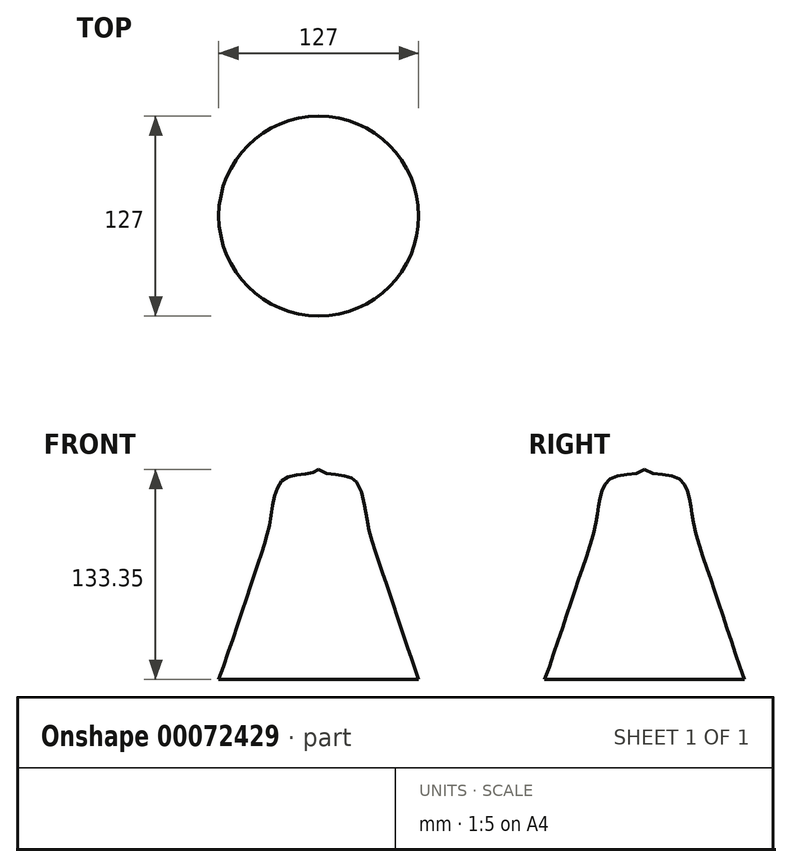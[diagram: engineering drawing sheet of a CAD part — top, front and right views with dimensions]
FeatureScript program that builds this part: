
annotation { "Feature Type Name" : "Feature", "Feature Type Description" : "" }
export const myFeature = defineFeature(function(context is Context, id is Id, definition is map)
    precondition{}
    {
        {
            var Q0;
            Q0=qCreatedBy(makeId("Front.planeOp"),FACE);
            var sketch = newSketch(context, id + "F0", { "sketchPlane" : qUnion([Q0])});
            skLineSegment(sketch, "E0", {"start": v(0, 58.39) * mm, "end": v(0, -74.96) * mm, "construction": true});
            skLineSegment(sketch, "E1.0", {"start": v(-63.5, 76.01) * mm, "end": v(-63.5, -74.96) * mm, "construction": true});
            skFitSpline(sketch, "E2", {"points": [v(-63.5, -74.96) * mm, v(-41.1, -8.94) * mm, v(-30.6, 26.81) * mm, v(-21.34, 52.67) * mm, v(0, 58.39) * mm], "startDerivative": vector(68.52, 189.13) * mm, "endDerivative": vector(57.47, 66.35) * mm});
            skSolve(sketch);
        }
        {
            var Q0;
            Q0=sQuery(id+"F0.wireOp",EDGE,"E2");
            var Q1;
            Q1=sQuery(id+"F0.wireOp",EDGE,"E0");
            revolve(context, id + "F1", {"bodyType" : ToolBodyType.SURFACE, "surfaceEntities" : qUnion([Q0]), "axis" : qUnion([Q1]), "revolveType" : RevolveType.FULL});
        }
    });
